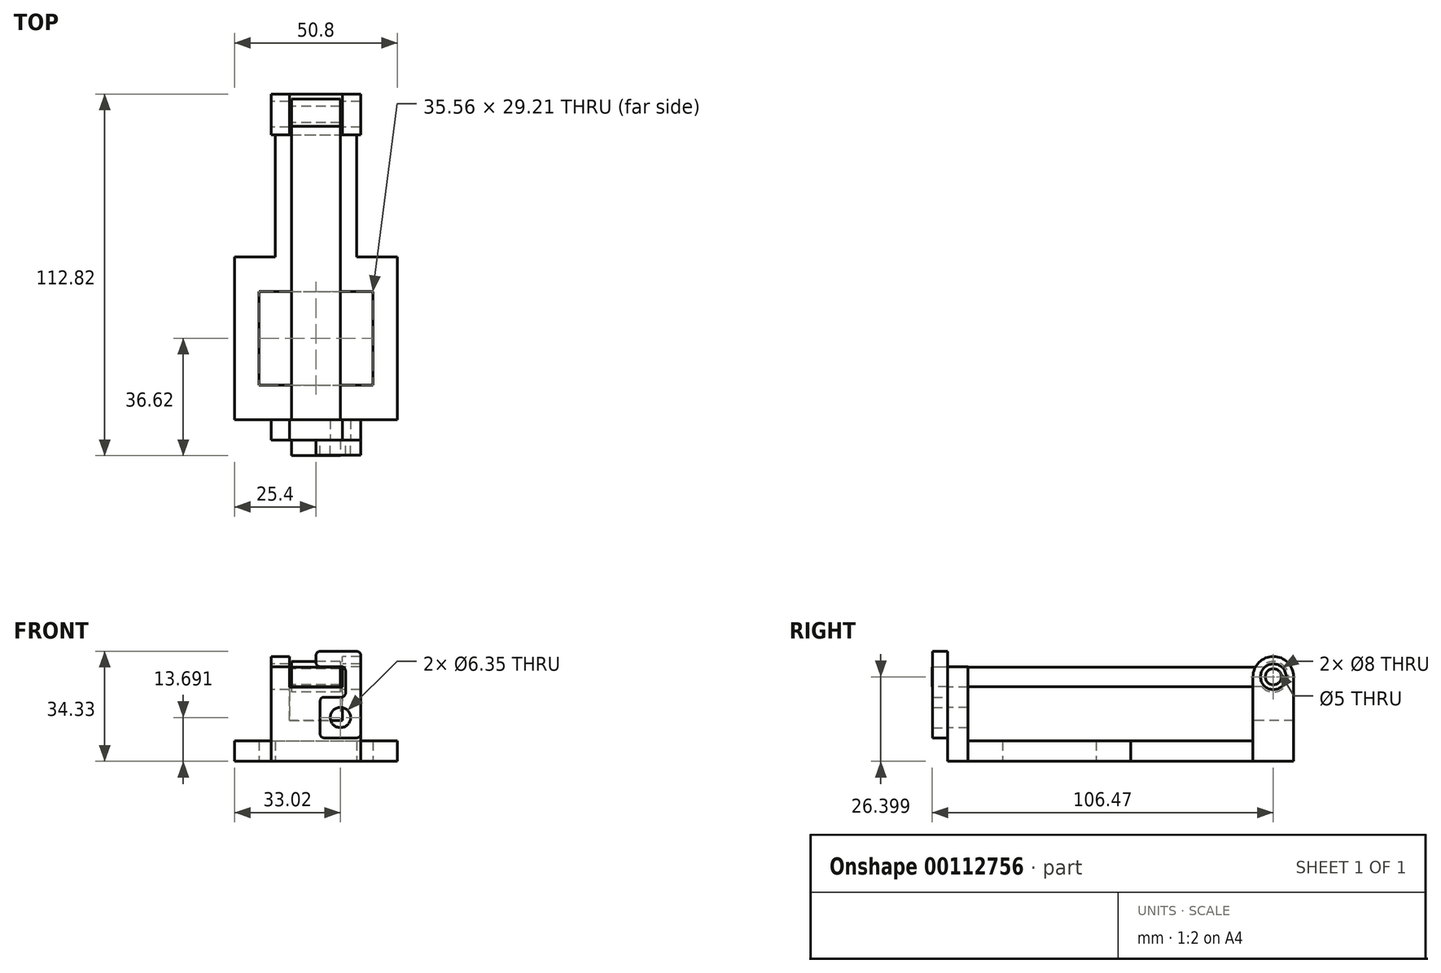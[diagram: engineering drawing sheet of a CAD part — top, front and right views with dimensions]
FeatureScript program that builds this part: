
annotation { "Feature Type Name" : "Feature", "Feature Type Description" : "" }
export const myFeature = defineFeature(function(context is Context, id is Id, definition is map)
    precondition{}
    {
        {
            var Q0;
            Q0=qCreatedBy(makeId("Top.planeOp"),FACE);
            var sketch = newSketch(context, id + "F0", { "sketchPlane" : qUnion([Q0])});
            skLineSegment(sketch, "E0.bottom", {"start": v(-25.4, 25.4) * mm, "end": v(-12.7, 25.4) * mm});
            skLineSegment(sketch, "E0.top", {"start": v(-25.4, -25.4) * mm, "end": v(25.4, -25.4) * mm});
            skLineSegment(sketch, "E0.left", {"start": v(-25.4, 25.4) * mm, "end": v(-25.4, -25.4) * mm});
            skLineSegment(sketch, "E0.right", {"start": v(25.4, 25.4) * mm, "end": v(25.4, -25.4) * mm});
            skPoint(sketch, "E0.middle", {"position": v(0, 0) * mm});
            skLineSegment(sketch, "E1.bottom", {"start": v(-17.78, 14.6) * mm, "end": v(17.78, 14.6) * mm});
            skLineSegment(sketch, "E1.top", {"start": v(-17.78, -14.6) * mm, "end": v(17.78, -14.6) * mm});
            skLineSegment(sketch, "E1.left", {"start": v(-17.78, 14.6) * mm, "end": v(-17.78, -14.6) * mm});
            skLineSegment(sketch, "E1.right", {"start": v(17.78, 14.6) * mm, "end": v(17.78, -14.6) * mm});
            skLineSegment(sketch, "E2", {"start": v(-12.7, 25.4) * mm, "end": v(-12.7, 63.5) * mm});
            skLineSegment(sketch, "E3", {"start": v(-12.7, 63.5) * mm, "end": v(12.7, 63.5) * mm});
            skLineSegment(sketch, "E4", {"start": v(12.7, 63.5) * mm, "end": v(12.7, 25.4) * mm});
            skLineSegment(sketch, "E5.trimOffspring", {"start": v(12.7, 25.4) * mm, "end": v(25.4, 25.4) * mm});
            skSolve(sketch);
        }
        {
            var Q0;
            Q0=makeQuery(id+"F0.imprint","IMPRINT",FACE,{"disambiguationData":[TD([[makeQuery(id+"F0.imprint","IMPRINT",EDGE,{"derivedFrom":sQuery(id+"F0.wireOp",EDGE,"E0.bottom")}),-1.0]])]});
            extrude(context, id + "F1", {"entities" : qUnion([Q0]), "depth" : 6.35 * mm});
        }
        {
            var Q0;
            Q0=qCreatedBy(makeId("Right.planeOp"),FACE);
            var sketch = newSketch(context, id + "F2", { "sketchPlane" : qUnion([Q0])});
            skCircle(sketch, "E6", {"center": v(69.85, 26.4) * mm, "radius": 4 * mm});
            skArc(sketch, "E7", {"start": v(76.2, 26.4) * mm, "mid": v(69.85, 32.75) * mm, "end": v(63.5, 26.4) * mm});
            skLineSegment(sketch, "E8", {"start": v(76.2, 26.4) * mm, "end": v(76.2, 0) * mm});
            skLineSegment(sketch, "E9", {"start": v(76.2, 0) * mm, "end": v(63.5, 0) * mm});
            skLineSegment(sketch, "E10", {"start": v(63.5, 26.4) * mm, "end": v(63.5, 0) * mm});
            skLineSegment(sketch, "E11", {"start": v(-25.4, 0) * mm, "end": v(-31.75, 0) * mm});
            skLineSegment(sketch, "E12", {"start": v(-31.75, 0) * mm, "end": v(-31.75, 29.57) * mm});
            skLineSegment(sketch, "E13", {"start": v(-31.75, 29.57) * mm, "end": v(-25.4, 29.57) * mm});
            skLineSegment(sketch, "E14", {"start": v(-25.4, 29.57) * mm, "end": v(-25.4, 0) * mm});
            skSolve(sketch);
        }
        {
            var Q0;
            Q0 = qSketchRegion(id + "F2", true);
            extrude(context, id + "F3", {"entities" : qUnion([Q0]), "operationType" : NewBodyOperationType.ADD, "depth" : 13.97 * mm, "hasSecondDirection" : true, "secondDirectionOppositeDirection" : true, "secondDirectionDepth" : 13.97 * mm});
        }
        {
            var Q0;
            Q0=makeQuery(id+"F3.opExtrude","SWEPT_FACE",FACE,{"disambiguationData":[OSD([sQuery(id+"F2.wireOp",EDGE,"E10")])]});
            var sketch = newSketch(context, id + "F4", { "sketchPlane" : qUnion([Q0])});
            skLineSegment(sketch, "E15.bottom", {"start": v(-8.26, 12.7) * mm, "end": v(8.25, 12.7) * mm});
            skLineSegment(sketch, "E15.top", {"start": v(-8.26, 38.1) * mm, "end": v(8.25, 38.1) * mm});
            skLineSegment(sketch, "E15.left", {"start": v(-8.26, 12.7) * mm, "end": v(-8.26, 38.1) * mm});
            skLineSegment(sketch, "E15.right", {"start": v(8.25, 12.7) * mm, "end": v(8.25, 38.1) * mm});
            skPoint(sketch, "E15.middle", {"position": v(0, 25.4) * mm});
            skSolve(sketch);
        }
        {
            var Q0;
            {var subQ0=sQuery(id+"F4.wireOp",EDGE,"E15.top");Q0=makeQuery(id+"F4.imprint","IMPRINT",FACE,{"disambiguationData":[TD([[makeQuery(id+"F4.imprint","IMPRINT",EDGE,{"derivedFrom":subQ0}),-1.0]])]});}
            var Q1;
            {var subQ0=sQuery(id+"F4.wireOp",EDGE,"E15.bottom");Q1=makeQuery(id+"F4.imprint","IMPRINT",FACE,{"disambiguationData":[TD([[makeQuery(id+"F4.imprint","IMPRINT",EDGE,{"derivedFrom":subQ0}),1.0]])]});}
            extrude(context, id + "F5", {"entities" : qUnion([Q0, Q1]), "operationType" : NewBodyOperationType.REMOVE, "endBound" : BoundingType.THROUGH_ALL, "oppositeDirection" : true, "depth" : 25.4 * mm});
        }
        {
            var Q0;
            Q0=qCreatedBy(makeId("Right.planeOp"),FACE);
            var sketch = newSketch(context, id + "F6", { "sketchPlane" : qUnion([Q0])});
            skCircle(sketch, "E16", {"center": v(69.85, 26.4) * mm, "radius": 2.5 * mm});
            skArc(sketch, "E17", {"start": v(66.2, 23.35) * mm, "mid": v(74.61, 26.4) * mm, "end": v(66.2, 29.45) * mm});
            skLineSegment(sketch, "E18", {"start": v(66.2, 29.45) * mm, "end": v(-36.62, 29.45) * mm});
            skLineSegment(sketch, "E19", {"start": v(66.2, 23.35) * mm, "end": v(-36.62, 23.35) * mm});
            skLineSegment(sketch, "E20", {"start": v(-36.62, 29.45) * mm, "end": v(-36.62, 23.35) * mm});
            skLineSegment(sketch, "E21", {"start": v(69.85, 26.4) * mm, "end": v(6.57, 26.4) * mm, "construction": true});
            skSolve(sketch);
        }
        {
            var Q0;
            Q0 = qSketchRegion(id + "F6", true);
            extrude(context, id + "F7", {"entities" : qUnion([Q0]), "depth" : 7.62 * mm, "hasSecondDirection" : true, "secondDirectionOppositeDirection" : true, "secondDirectionDepth" : 7.62 * mm});
        }
        {
            var Q0;
            Q0=makeQuery(id+"F3.opExtrude","SWEPT_FACE",FACE,{"disambiguationData":[OSD([sQuery(id+"F2.wireOp",EDGE,"E12")])]});
            var sketch = newSketch(context, id + "F8", { "sketchPlane" : qUnion([Q0])});
            skLineSegment(sketch, "E22.bottom", {"start": v(8.26, 29.57) * mm, "end": v(-8.26, 29.57) * mm});
            skLineSegment(sketch, "E22.top", {"start": v(8.26, 23.22) * mm, "end": v(-8.26, 23.22) * mm});
            skLineSegment(sketch, "E22.left", {"start": v(8.26, 29.57) * mm, "end": v(8.26, 23.22) * mm});
            skLineSegment(sketch, "E22.right", {"start": v(-8.26, 29.57) * mm, "end": v(-8.26, 23.22) * mm});
            skPoint(sketch, "E22.middle", {"position": v(0, 26.4) * mm});
            skSolve(sketch);
        }
        {
            var Q0;
            Q0=makeQuery(id+"F8.imprint","IMPRINT",FACE,{"disambiguationData":[TD([[makeQuery(id+"F8.imprint","IMPRINT",EDGE,{"derivedFrom":sQuery(id+"F8.wireOp",EDGE,"E22.bottom")}),1.0]])]});
            extrude(context, id + "F9", {"entities" : qUnion([Q0]), "operationType" : NewBodyOperationType.REMOVE, "endBound" : BoundingType.UP_TO_NEXT, "oppositeDirection" : true, "depth" : 25.4 * mm});
        }
        {
            var Q0;
            Q0=makeQuery(id+"F3.opExtrude","SWEPT_FACE",FACE,{"disambiguationData":[OSD([sQuery(id+"F2.wireOp",EDGE,"E12")])]});
            var sketch = newSketch(context, id + "F10", { "sketchPlane" : qUnion([Q0])});
            skCircle(sketch, "E23", {"center": v(7.62, 13.7) * mm, "radius": 3.18 * mm});
            skLineSegment(sketch, "E24", {"start": v(0, 30.84) * mm, "end": v(0, 33.06) * mm});
            skLineSegment(sketch, "E25", {"start": v(1.27, 34.33) * mm, "end": v(12.7, 34.33) * mm});
            skLineSegment(sketch, "E26", {"start": v(13.97, 33.06) * mm, "end": v(13.97, 8.61) * mm});
            skLineSegment(sketch, "E27", {"start": v(12.7, 7.34) * mm, "end": v(2.54, 7.34) * mm});
            skLineSegment(sketch, "E28", {"start": v(1.27, 8.61) * mm, "end": v(1.27, 18.77) * mm});
            skLineSegment(sketch, "E29", {"start": v(2.54, 20.04) * mm, "end": v(7.94, 20.04) * mm});
            skLineSegment(sketch, "E30", {"start": v(9.2, 21.31) * mm, "end": v(9.2, 28.3) * mm});
            skLineSegment(sketch, "E31", {"start": v(7.94, 29.57) * mm, "end": v(1.27, 29.57) * mm});
            skLineSegment(sketch, "E32", {"start": v(13.97, 7.34) * mm, "end": v(1.27, 20.04) * mm, "construction": true});
            skPoint(sketch, "E33.visualSharp", {"position": v(9.2, 20.04) * mm});
            skArc(sketch, "E33.filletArc", {"start": v(7.94, 20.04) * mm, "mid": v(8.84, 20.41) * mm, "end": v(9.2, 21.31) * mm});
            skPoint(sketch, "E34.visualSharp", {"position": v(13.97, 7.34) * mm});
            skArc(sketch, "E34.filletArc", {"start": v(12.7, 7.34) * mm, "mid": v(13.6, 7.71) * mm, "end": v(13.97, 8.61) * mm});
            skPoint(sketch, "E35.visualSharp", {"position": v(1.27, 7.34) * mm});
            skArc(sketch, "E35.filletArc", {"start": v(1.27, 8.61) * mm, "mid": v(1.64, 7.71) * mm, "end": v(2.54, 7.34) * mm});
            skPoint(sketch, "E36.visualSharp", {"position": v(1.27, 20.04) * mm});
            skArc(sketch, "E36.filletArc", {"start": v(2.54, 20.04) * mm, "mid": v(1.64, 19.67) * mm, "end": v(1.27, 18.77) * mm});
            skPoint(sketch, "E37.visualSharp", {"position": v(13.97, 34.33) * mm});
            skArc(sketch, "E37.filletArc", {"start": v(13.97, 33.06) * mm, "mid": v(13.6, 33.96) * mm, "end": v(12.7, 34.33) * mm});
            skPoint(sketch, "E38.visualSharp", {"position": v(9.2, 29.57) * mm});
            skArc(sketch, "E38.filletArc", {"start": v(9.2, 28.3) * mm, "mid": v(8.84, 29.2) * mm, "end": v(7.94, 29.57) * mm});
            skPoint(sketch, "E39.visualSharp", {"position": v(0, 29.57) * mm});
            skArc(sketch, "E39.filletArc", {"start": v(0, 30.84) * mm, "mid": v(0.37, 29.94) * mm, "end": v(1.27, 29.57) * mm});
            skPoint(sketch, "E40.visualSharp", {"position": v(0, 34.33) * mm});
            skArc(sketch, "E40.filletArc", {"start": v(1.27, 34.33) * mm, "mid": v(0.37, 33.96) * mm, "end": v(0, 33.06) * mm});
            skSolve(sketch);
        }
        {
            var Q0;
            Q0=makeQuery(id+"F10.imprint","IMPRINT",FACE,{"disambiguationData":[TD([[makeQuery(id+"F10.imprint","IMPRINT",EDGE,{"derivedFrom":sQuery(id+"F10.wireOp",EDGE,"E23")}),-1.0]])]});
            var Q1;
            Q1=makeQuery(id+"F10.imprint","IMPRINT",FACE,{"disambiguationData":[TD([[makeQuery(id+"F10.imprint","IMPRINT",EDGE,{"derivedFrom":sQuery(id+"F10.wireOp",EDGE,"E24")}),-1.0]])]});
            extrude(context, id + "F11", {"entities" : qUnion([Q0, Q1]), "depth" : 4.76 * mm});
        }
        {
            var Q0;
            Q0=makeQuery(id+"F10.imprint","IMPRINT",FACE,{"disambiguationData":[TD([[makeQuery(id+"F10.imprint","IMPRINT",EDGE,{"derivedFrom":sQuery(id+"F10.wireOp",EDGE,"E23")}),1.0]])]});
            var Q1;
            Q1=makeQuery(id+"F3.opExtrude","SWEPT_FACE",FACE,{"disambiguationData":[OSD([sQuery(id+"F2.wireOp",EDGE,"E14")])]});
            extrude(context, id + "F12", {"entities" : qUnion([Q0]), "operationType" : NewBodyOperationType.REMOVE, "endBound" : BoundingType.UP_TO_SURFACE, "oppositeDirection" : true, "endBoundEntityFace" : qUnion([Q1]), "depth" : 25.4 * mm});
        }
    });
